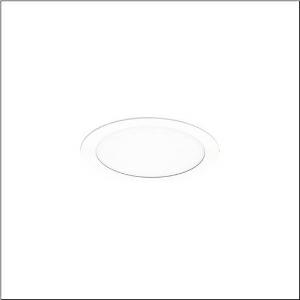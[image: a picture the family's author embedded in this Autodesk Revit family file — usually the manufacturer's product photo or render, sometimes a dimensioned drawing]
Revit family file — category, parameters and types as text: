
# Revit family: lunis_21_l_51db16td91c
name_source: partatom
category: Lighting Fixtures
units: mm (PartAtom-declared; Revit-internal decimal feet)

## family parameters
Cut with Voids When Loaded = No
Host = Face
Light Source = No
Part Type = Normal
Room Calculation Point = No
Round Connector Dimension = Use Diameter
Shared = No

## types (1)
- --- (1 x LED 3000 K ... 6500 K, 3290 lm, 25.4 W, 4000K)
    Apparent Load = 25 VA
    CIE Flux Codes = 50 80 96 100 100
    Color Rendering = 80
    Color Temperature = 4000K
    Default Elevation = 1800 mm
    Description = Lunis 21,  L, downlight, light control with lens, of PMMA, optical cover: cover panel, of PC, opal, light emission: direct distribution, LED rated luminous flux: 3.290lm, light colour: 8tw, with terminal, 5-pole, mains connection: 220..240V, AC/DC, 0/50..60Hz, housing, round, of diecast aluminium, traffic white (RAL 9016), diameter: 165mm, clamping range: 1..40mm, protection rating (complete): IP20, protection rating (on room side): IP54, insulation class (complete): insulation class II (safety insulation), certification: CE, impact resistance: IK03, packaging unit: 1 piece
    Height = 0 mm  [stored 0 ft]
    Lamp = 1 x LED 3000 K ... 6500 K
    Lamp Light Flux = 3290 lm
    Lamp Power = 25.4 W
    Lamp count = 1
    Length = 165 mm
    Luminous efficacy = 130 lm/W
    Manufacturer = Siteco
    ModVariant = No
    Model = 51DB16TD91C
    Mounting Place = Ceiling
    Mounting Type = Recessed
    Number of Poles = 1
    OnlyDefault = Yes
    Power Factor = 1
    Product Name = Lunis 21 L
    Product group = downlight
    ProductGroupID = 400
    Protection Class = Protection class II
    Protection Degree = IP 20
    RLX_Detail_Level = 1
    RLX_Emergency_Light_Flux = 0 lm
    RLX_Emergency_Type = 0
    RLX_Emergency_Type_DB = No
    RlxData = <blob elided: 12445 chars, md5=a5b214bf>
    Socket = socket
    Standby Power = 0 W
    System Light Flux = 3290 lm
    System Power = 25 W
    Type Comments = individual setting: CCT=4000K, colour temperature 4000K, luminous flux: 100 % | (ON | ON | OFF | OFF) | 700 mA
    Type Image = l_1291165.jpg
    URL = http://relux.com
    VarID = @adj_020756
    Voltage = 0 V
    Weight = 0.00 kg
    Width = 0 mm  [stored 0 ft]

note: [stored X ft] marks values corroborated as IEEE doubles in the binary element streams (Revit-internal decimal feet)

## geometry (parser evidence)
native form markers: Sweep x9
no freeform markers — native parametric forms only
